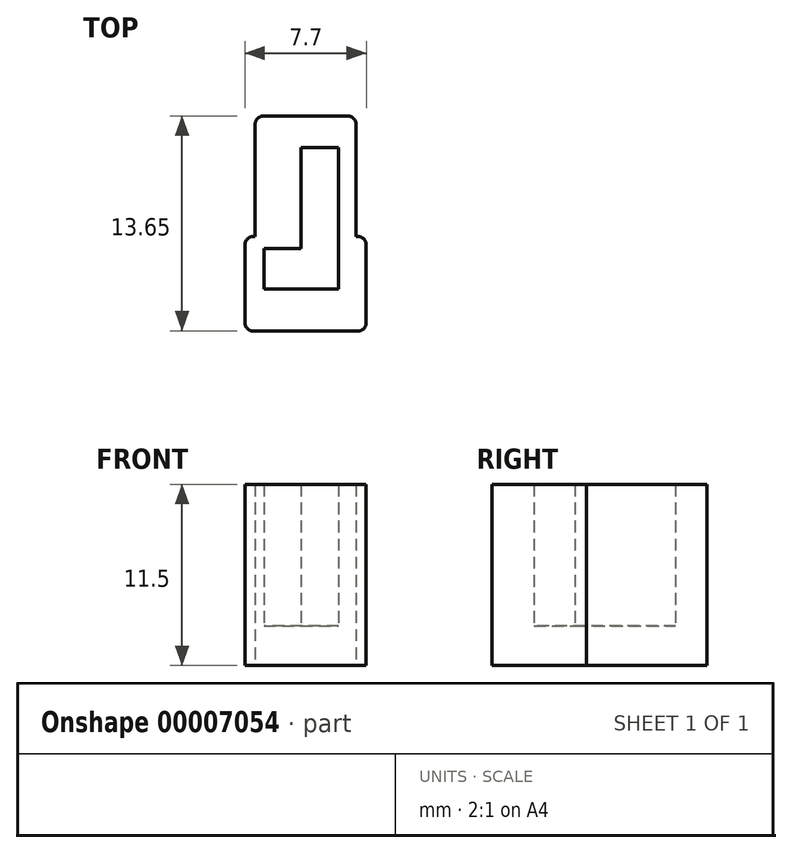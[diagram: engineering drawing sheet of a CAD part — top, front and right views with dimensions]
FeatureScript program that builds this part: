
annotation { "Feature Type Name" : "Feature", "Feature Type Description" : "" }
export const myFeature = defineFeature(function(context is Context, id is Id, definition is map)
    precondition{}
    {
        {
            var Q0;
            Q0=qCreatedBy(makeId("Top.planeOp"),FACE);
            var sketch = newSketch(context, id + "F0", { "sketchPlane" : qUnion([Q0])});
            skLineSegment(sketch, "E0", {"start": v(-39.6, -33.1) * mm, "end": v(-39.6, -26.7) * mm});
            skLineSegment(sketch, "E1", {"start": v(-39.6, -26.7) * mm, "end": v(-37.2, -26.7) * mm});
            skLineSegment(sketch, "E2", {"start": v(-42.65, -38.35) * mm, "end": v(-35.95, -38.35) * mm});
            skLineSegment(sketch, "E3", {"start": v(-35.45, -37.85) * mm, "end": v(-35.45, -32.85) * mm});
            skLineSegment(sketch, "E4", {"start": v(-36.6, -24.7) * mm, "end": v(-42, -24.7) * mm});
            skLineSegment(sketch, "E5", {"start": v(-35.95, -32.35) * mm, "end": v(-36.1, -32.35) * mm});
            skLineSegment(sketch, "E6", {"start": v(-36.1, -32.35) * mm, "end": v(-36.1, -25.2) * mm});
            skLineSegment(sketch, "E7", {"start": v(-37.2, -26.7) * mm, "end": v(-37.2, -35.7) * mm});
            skLineSegment(sketch, "E8", {"start": v(-37.2, -35.7) * mm, "end": v(-41.95, -35.7) * mm});
            skLineSegment(sketch, "E9", {"start": v(-41.95, -35.7) * mm, "end": v(-41.95, -33.1) * mm});
            skLineSegment(sketch, "E10", {"start": v(-41.95, -33.1) * mm, "end": v(-39.6, -33.1) * mm});
            skLineSegment(sketch, "E11", {"start": v(-42.5, -25.2) * mm, "end": v(-42.5, -32.35) * mm});
            skLineSegment(sketch, "E12", {"start": v(-42.5, -32.35) * mm, "end": v(-42.65, -32.35) * mm});
            skLineSegment(sketch, "E13", {"start": v(-43.15, -32.85) * mm, "end": v(-43.15, -37.85) * mm});
            skPoint(sketch, "E14.visualSharp", {"position": v(-35.45, -32.35) * mm});
            skArc(sketch, "E14.filletArc", {"start": v(-35.45, -32.85) * mm, "mid": v(-35.6, -32.5) * mm, "end": v(-35.95, -32.35) * mm});
            skPoint(sketch, "E15.visualSharp", {"position": v(-35.45, -38.35) * mm});
            skArc(sketch, "E15.filletArc", {"start": v(-35.95, -38.35) * mm, "mid": v(-35.6, -38.2) * mm, "end": v(-35.45, -37.85) * mm});
            skPoint(sketch, "E16.visualSharp", {"position": v(-43.15, -38.35) * mm});
            skArc(sketch, "E16.filletArc", {"start": v(-43.15, -37.85) * mm, "mid": v(-43, -38.2) * mm, "end": v(-42.65, -38.35) * mm});
            skPoint(sketch, "E17.visualSharp", {"position": v(-43.15, -32.35) * mm});
            skArc(sketch, "E17.filletArc", {"start": v(-42.65, -32.35) * mm, "mid": v(-43, -32.5) * mm, "end": v(-43.15, -32.85) * mm});
            skPoint(sketch, "E18.visualSharp", {"position": v(-36.1, -24.7) * mm});
            skArc(sketch, "E18.filletArc", {"start": v(-36.1, -25.2) * mm, "mid": v(-36.25, -24.85) * mm, "end": v(-36.6, -24.7) * mm});
            skPoint(sketch, "E19.visualSharp", {"position": v(-42.5, -24.7) * mm});
            skArc(sketch, "E19.filletArc", {"start": v(-42, -24.7) * mm, "mid": v(-42.36, -24.85) * mm, "end": v(-42.5, -25.2) * mm});
            skSolve(sketch);
        }
        {
            var Q0;
            Q0=makeQuery(id+"F0.imprint","IMPRINT",FACE,{"disambiguationData":[TD([[makeQuery(id+"F0.imprint","IMPRINT",EDGE,{"derivedFrom":sQuery(id+"F0.wireOp",EDGE,"E0")}),1.0]])]});
            extrude(context, id + "F1", {"entities" : qUnion([Q0]), "depth" : 9 * mm});
        }
        {
            var Q0;
            Q0=makeQuery(id+"F0.imprint","IMPRINT",FACE,{"disambiguationData":[TD([[makeQuery(id+"F0.imprint","IMPRINT",EDGE,{"derivedFrom":sQuery(id+"F0.wireOp",EDGE,"E0")}),-1.0]])]});
            var Q1;
            Q1=makeQuery(id+"F0.imprint","IMPRINT",FACE,{"disambiguationData":[TD([[makeQuery(id+"F0.imprint","IMPRINT",EDGE,{"derivedFrom":sQuery(id+"F0.wireOp",EDGE,"E0")}),1.0]])]});
            extrude(context, id + "F2", {"entities" : qUnion([Q0, Q1]), "operationType" : NewBodyOperationType.ADD, "oppositeDirection" : true, "depth" : 2.5 * mm});
        }
    });
